# Revit family: STC_A3-Beam-Precast-L-Shaped-(M)
name_source: partatom
category: Structural Framing
revit_build: Autodesk Revit 2016 (Build: 20150220_1215(x64)
units: mm (PartAtom-declared; Revit-internal decimal feet)

## family parameters
Always export as geometry = No
Always vertical = Yes
Cut with Voids When Loaded = No
Display in Hidden Views = Edges Hidden by Other Members
Material for Model Behavior = Precast Concrete
Section Shape = Not Defined
Shared = No
Show family pre-cut in plan views = Yes

## types (3) — shared parameters
Seat = 150 mm
b = 450 mm  [stored 1.47638 ft]

## per-type parameters (varying)
| type | h | h1 |
| 450 LB 500 Beams | 500 mm  [stored 1.64042 ft] | 300 mm |
| 450 LB 600 Beams | 600 mm | 300 mm |
| 450 LB 1200 Baems | 1200 mm | 800 mm  [stored 2.62467 ft] |

note: [stored X ft] marks values corroborated as IEEE doubles in the binary element streams (Revit-internal decimal feet)

## geometry (parser evidence)
native form markers: Sweep x2
no freeform markers — native parametric forms only
